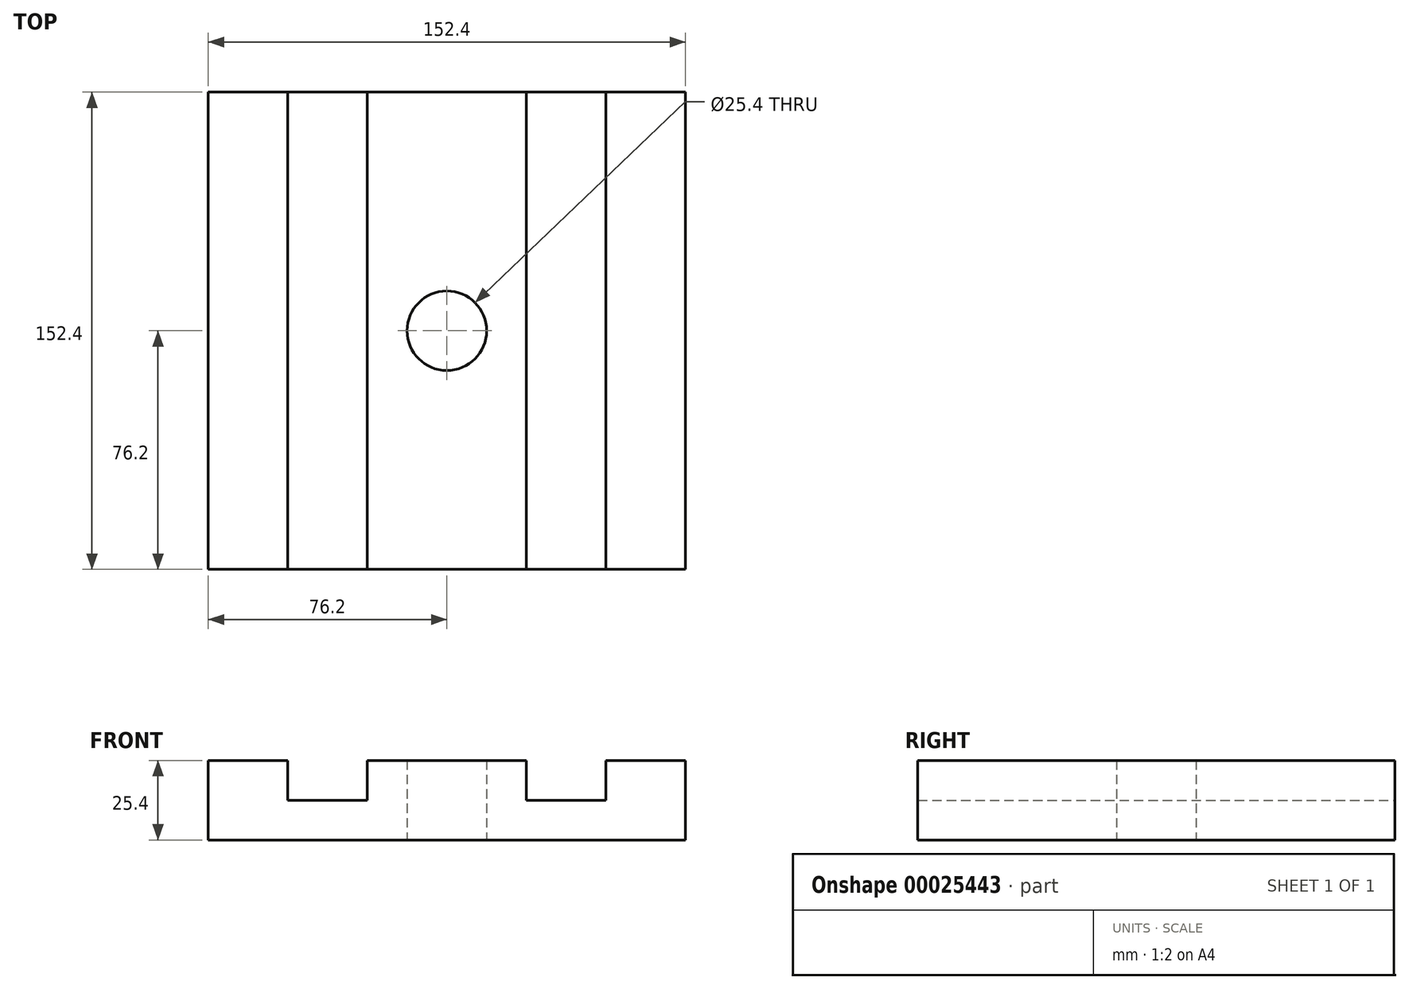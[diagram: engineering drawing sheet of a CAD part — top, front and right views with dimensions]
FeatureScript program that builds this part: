
annotation { "Feature Type Name" : "Feature", "Feature Type Description" : "" }
export const myFeature = defineFeature(function(context is Context, id is Id, definition is map)
    precondition{}
    {
        {
            var Q0;
            Q0=qCreatedBy(makeId("Top.planeOp"),FACE);
            var sketch = newSketch(context, id + "F0", { "sketchPlane" : qUnion([Q0])});
            skCircle(sketch, "E0", {"center": v(0, 0) * mm, "radius": 12.7 * mm});
            skLineSegment(sketch, "E1.rect.bottom", {"start": v(76.2, 76.2) * mm, "end": v(-76.2, 76.2) * mm});
            skLineSegment(sketch, "E1.rect.top", {"start": v(76.2, -76.2) * mm, "end": v(-76.2, -76.2) * mm});
            skLineSegment(sketch, "E1.rect.left", {"start": v(76.2, 76.2) * mm, "end": v(76.2, -76.2) * mm});
            skLineSegment(sketch, "E1.rect.right", {"start": v(-76.2, 76.2) * mm, "end": v(-76.2, -76.2) * mm});
            skSolve(sketch);
        }
        {
            var Q0;
            Q0=makeQuery(id+"F0.imprint","IMPRINT",FACE,{"disambiguationData":[TD([[makeQuery(id+"F0.imprint","IMPRINT",EDGE,{"derivedFrom":sQuery(id+"F0.wireOp",EDGE,"E0")}),-1.0]])]});
            extrude(context, id + "F1", {"entities" : qUnion([Q0]), "depth" : 25.4 * mm});
        }
        {
            var Q0;
            Q0=makeQuery(id+"F1.opExtrude","CAP_FACE",FACE,{"disambiguationData":[OSD([sQuery(id+"F0.wireOp",EDGE,"E0"),sQuery(id+"F0.wireOp",EDGE,"E1.rect.bottom"),sQuery(id+"F0.wireOp",EDGE,"E1.rect.top"),sQuery(id+"F0.wireOp",EDGE,"E1.rect.left"),sQuery(id+"F0.wireOp",EDGE,"E1.rect.right")])],"isStart":false});
            var sketch = newSketch(context, id + "F2", { "sketchPlane" : qUnion([Q0])});
            skLineSegment(sketch, "E2.bottom", {"start": v(-50.8, 76.2) * mm, "end": v(-25.4, 76.2) * mm});
            skLineSegment(sketch, "E2.top", {"start": v(-50.8, -76.2) * mm, "end": v(-25.4, -76.2) * mm});
            skLineSegment(sketch, "E2.left", {"start": v(-50.8, 76.2) * mm, "end": v(-50.8, -76.2) * mm});
            skLineSegment(sketch, "E2.right", {"start": v(-25.4, 76.2) * mm, "end": v(-25.4, -76.2) * mm});
            skLineSegment(sketch, "E3.bottom", {"start": v(25.4, -76.2) * mm, "end": v(50.8, -76.2) * mm});
            skLineSegment(sketch, "E3.top", {"start": v(25.4, 76.2) * mm, "end": v(50.8, 76.2) * mm});
            skLineSegment(sketch, "E3.left", {"start": v(25.4, -76.2) * mm, "end": v(25.4, 76.2) * mm});
            skLineSegment(sketch, "E3.right", {"start": v(50.8, -76.2) * mm, "end": v(50.8, 76.2) * mm});
            skSolve(sketch);
        }
        {
            var Q0;
            Q0 = qSketchRegion(id + "F2", true);
            extrude(context, id + "F3", {"entities" : qUnion([Q0]), "operationType" : NewBodyOperationType.REMOVE, "oppositeDirection" : true, "depth" : 12.7 * mm});
        }
    });
